# Revit family: Upton Chairs
name_source: partatom
category: Furniture
units: mm (PartAtom-declared; Revit-internal decimal feet)

## family parameters
Always vertical = Yes
Cut with Voids When Loaded = No
OmniClass Number = 23.40.20.00
OmniClass Title = General Furniture and Specialties
Room Calculation Point = No
Shared = No
Work Plane-Based = No

## types (6) — shared parameters
Manufacturer = AIS Inc
Product = UPTON CHAIRS
URL = https://www.ais-inc.com
zero-valued in all types: Default Elevation

## per-type parameters (varying)
| type | Description | Model |
| 4700C-1D Arms | Configurable Task Chair with 1D Arms | 4700C |
| 4700C-Fixed Arms | Configurable Task Chair with Fixed Arms | 4700C |
| 4700C-No Arms | Configurable Task Chair with No Arms | 4700C |
| 4700MMC-1D Arms | Configurable Mesh Task Chair with 1D Arms | 4700MMC |
| 4700MMC-Fixed Arms | Configurable Mesh Task Chair with Fixed Arms | 4700MMC |
| 4700MMC-No Arms | Configurable Mesh Task Chair with No Arms | 4700MMC |

type visibility flags: 6 boolean params named "<type name>" — each type sets only its own to Yes (folded from table)

## geometry (parser evidence)
native form markers: Sweep x3
no freeform markers — native parametric forms only
